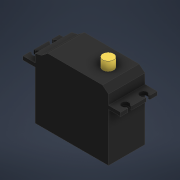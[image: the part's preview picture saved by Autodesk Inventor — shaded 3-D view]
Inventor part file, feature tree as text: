
AUTODESK INVENTOR PART (.ipt)
format: ipt  version: 2021 (Build 250183000, 183)  size: 165,888 bytes
history: native  units: mm
features: extrude x3, sketch x3, other x1
ambient origin geometry x8: Origin, YZ Plane, XZ Plane, XY Plane, X Axis, Y Axis, Z Axis, Center Point
bodies: Volumenkörper1 (feature_tree)
feature tree (7):
  other  "Servo"
  extrude  "Extrusion1"  Depth=26.6mm
  extrude  "Extrusion2"  Depth=10.0mm
  extrude  "Extrusion3"  Depth=5.0mm
  sketch  "Skizze1"  dims[d0=40.3mm d1=26.6mm]
  sketch  "Skizze2"  dims[d3=10.0mm d4=3.618671mm]
  sketch  "Skizze3"  dims[d5=3.402944mm d6=3.241736mm d7=18.036317mm d8=24.84032mm d9=24.604189mm d10=6.65mm d11=2.0mm d12=6.65mm d13=2.0mm d17=20.0mm d18=0.0mm d19=4.0mm d21=5.0mm d23=2.5mm d25=2.0mm d26=20.0mm d27=0.0mm d28=6.0mm d29=10.0mm d30=5.0mm d31=0.0mm]
